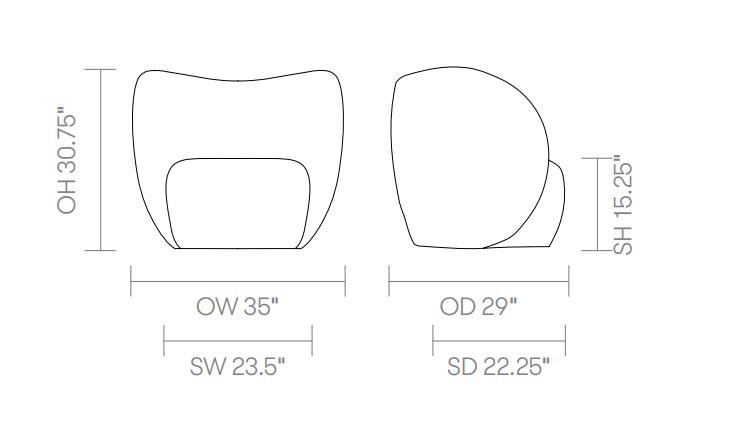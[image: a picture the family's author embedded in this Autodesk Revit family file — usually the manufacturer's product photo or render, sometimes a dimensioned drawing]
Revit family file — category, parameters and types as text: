
# Revit family: DBLTD_TheSenatorGroup_OfficeChairs_Bastille Lounge_US
name_source: partatom
category: Furniture
units: mm (PartAtom-declared; Revit-internal decimal feet)

## family parameters
Always vertical = Yes
Cut with Voids When Loaded = No
OmniClass Number = 23.40.20.00
OmniClass Title = General Furniture and Specialties
Render Appearance Source = Family Geometry
Room Calculation Point = No
Shared = Yes
Work Plane-Based = No

## types (3) — shared parameters
Assembly Code = E2020200
AssetType = Movable
Category = Pr_40_50_12_57 Office chairs
Color = Upholstery: Various.
Constituents = Frame, Seat and Back
DurationUnit = years
ExpectedLife = 5
Finish = Upholstery: Various.
Keynote = Pr_40_50_12_57 Office chairs
Manufacturer = The Senator Group
ManufacturerName = The Senator Group
ManufacturerURL = https://www.allermuir.com
Material = Moulded foam back rest, Cut foam seat carcass, Fully upholstered, Plastic glides
Name = Chair
ProductInformation = https://www.allermuir.com
SeatingHeight = 385 mm  [stored 1.26312 ft]
Shape = Rectangular
URL = https://www.thesenatorgroup.com
Uniclass2015Code = Pr_40_50_12_57
Uniclass2015Title = Office chairs
Uniclass2015Version = Products v1.15
Version = 1
WarrantyDescription = The Senator Group warrants that its manufactured products are free from manufacturing defects - in materials or workmanship - for a period of five (5) years.
WarrantyDurationLabor = 5
WarrantyDurationParts = 5
WarrantyDurationUnit = years
WarrantyGuarantorLabor = https://www.thesenatorgroup.com
WarrantyGuarantorParts = https://www.thesenatorgroup.com
zero-valued in all types: Cost, Default Elevation

## per-type parameters (varying)
| type | Model | ModelNumber | NominalDepth | NominalHeight | NominalWidth | SeatType | Size |
| 1 Seat Club Chair | BST100 | BST100 | 735 mm | 780 mm  [stored 2.55906 ft] | 890 mm  [stored 2.91995 ft] | Nestred_DBLTD_TheSenatorGroup_OfficeChairs_BastilleLounge_1 | 35 x 29 x 30.75 mm |
| 2 Seat Sofa | BST200 | BST200 | 835 mm | 790 mm  [stored 2.59186 ft] | 1810 mm  [stored 5.93832 ft] | Nestred_DBLTD_TheSenatorGroup_OfficeChairs_BastilleLounge_2 | 57.75 x 32.75 x 31 mm |
| 3 Seat Sofa | BST300 | BST300 | 920 mm  [stored 3.01837 ft] | 790 mm  [stored 2.59186 ft] | 2440 mm  [stored 8.00525 ft] | Nestred_DBLTD_TheSenatorGroup_OfficeChairs_BastilleLounge_3 | 84.25 x 36.25 x 31 mm |

note: column(s) folded — value = type name in every type: Description, ModelReference, Type Comments

note: [stored X ft] marks values corroborated as IEEE doubles in the binary element streams (Revit-internal decimal feet)

## geometry (parser evidence)
native form markers: Sweep x11
no freeform markers — native parametric forms only
